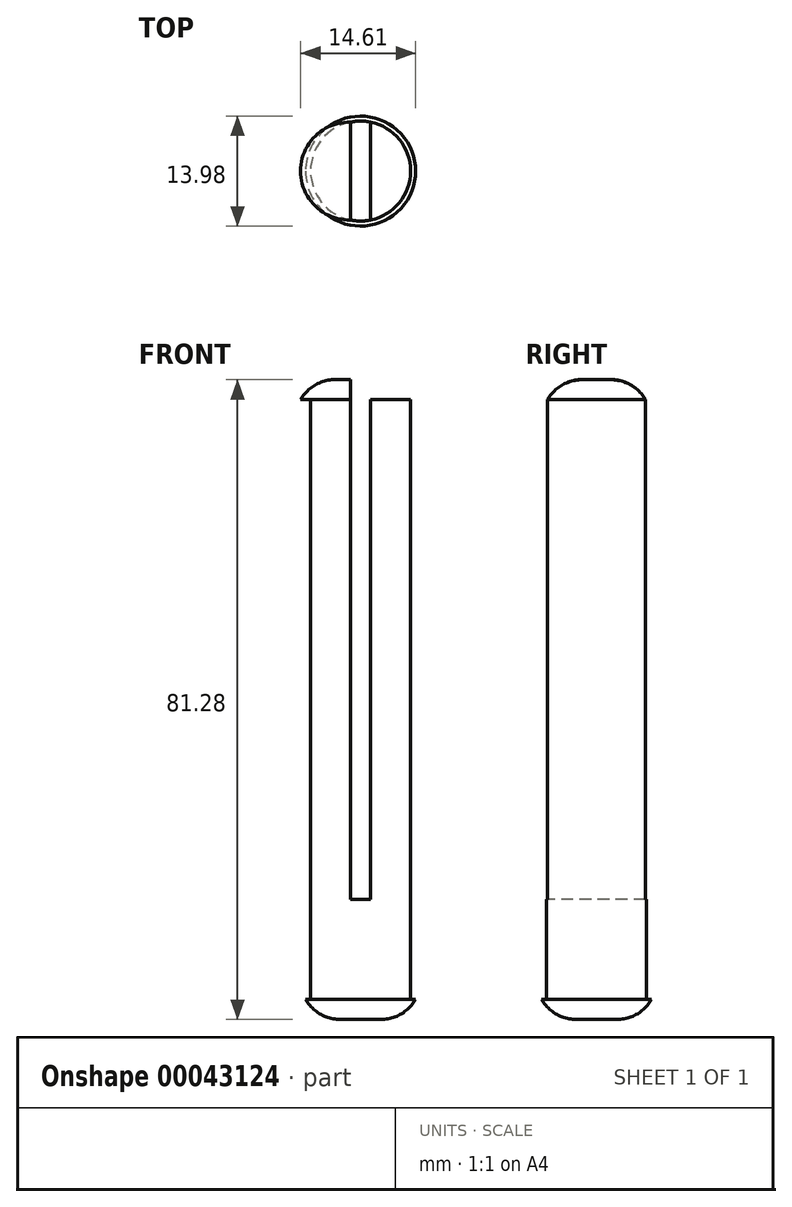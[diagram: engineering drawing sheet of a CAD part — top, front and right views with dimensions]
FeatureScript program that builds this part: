
annotation { "Feature Type Name" : "Feature", "Feature Type Description" : "" }
export const myFeature = defineFeature(function(context is Context, id is Id, definition is map)
    precondition{}
    {
        {
            var Q0;
            Q0=qCreatedBy(makeId("Top.planeOp"),FACE);
            var sketch = newSketch(context, id + "F0", { "sketchPlane" : qUnion([Q0])});
            skCircle(sketch, "E0", {"center": v(0, 0) * mm, "radius": 6.35 * mm});
            skSolve(sketch);
        }
        {
            var Q0;
            Q0=makeQuery(id+"F0.imprint","IMPRINT",FACE,{"disambiguationData":[TD([[makeQuery(id+"F0.imprint","IMPRINT",EDGE,{"derivedFrom":sQuery(id+"F0.wireOp",EDGE,"E0")}),1.0]])]});
            extrude(context, id + "F1", {"entities" : qUnion([Q0]), "depth" : 76.2 * mm});
        }
        {
            var Q0;
            Q0=makeQuery(id+"F1.opExtrude","CAP_FACE",FACE,{"disambiguationData":[OSD([sQuery(id+"F0.wireOp",EDGE,"E0")])],"isStart":false});
            var sketch = newSketch(context, id + "F2", { "sketchPlane" : qUnion([Q0])});
            skLineSegment(sketch, "E1.rect.bottom", {"start": v(1.27, 11.24) * mm, "end": v(-1.27, 11.24) * mm});
            skLineSegment(sketch, "E1.rect.top", {"start": v(1.27, -11.24) * mm, "end": v(-1.27, -11.24) * mm});
            skLineSegment(sketch, "E1.rect.left", {"start": v(1.27, 11.24) * mm, "end": v(1.27, -11.24) * mm});
            skLineSegment(sketch, "E1.rect.right", {"start": v(-1.27, 11.24) * mm, "end": v(-1.27, -11.24) * mm});
            skPoint(sketch, "E1.rect.middle", {"position": v(0, 0) * mm});
            skSolve(sketch);
        }
        {
            var Q0;
            {var subQ1=makeQuery(id+"F1.opExtrude","CAP_EDGE",EDGE,{"disambiguationData":[OSD([sQuery(id+"F0.wireOp",EDGE,"E0")])],"isStart":false});var subQ4=sQuery(id+"F2.wireOp",EDGE,"E1.rect.left");var subQ6=makeQuery(id+"F2.imprint","INTERSECT",VERTEX,{"disambiguationData":[OD(0.0)],"derivedFrom":[subQ1,subQ4]});Q0=makeQuery(id+"F2.imprint","IMPRINT",FACE,{"disambiguationData":[TD([[makeQuery(id+"F2.imprint","IMPRINT",EDGE,{"disambiguationData":[TD([[subQ6,-1.0]])],"derivedFrom":subQ4}),-1.0]])]});}
            extrude(context, id + "F3", {"entities" : qUnion([Q0]), "operationType" : NewBodyOperationType.REMOVE, "oppositeDirection" : true, "depth" : 63.5 * mm});
        }
        {
            var Q0;
            {var subQ0=sQuery(id+"F0.wireOp",EDGE,"E0");Q0=makeQuery(id+"F3.boolean.opBoolean","SPLIT",FACE,{"disambiguationData":[TD([makeQuery(id+"F3.opExtrude","SWEPT_FACE",FACE,{"disambiguationData":[OSD([sQuery(id+"F2.wireOp",EDGE,"E1.rect.right")])]})])],"derivedFrom":makeQuery(id+"F1.opExtrude","CAP_FACE",FACE,{"disambiguationData":[OSD([subQ0])],"isStart":false})});}
            var sketch = newSketch(context, id + "F4", { "sketchPlane" : qUnion([Q0])});
            skLineSegment(sketch, "E2", {"start": v(-8.9, 6.22) * mm, "end": v(-8.89, -19.18) * mm});
            skLineSegment(sketch, "E3", {"start": v(0, 6.22) * mm, "end": v(0, -19.9) * mm, "construction": true});
            skLineSegment(sketch, "E4.MirrorCS", {"start": v(8.9, 6.22) * mm, "end": v(8.89, -19.18) * mm});
            skArc(sketch, "E5", {"start": v(-1.27, 6.22) * mm, "mid": v(-7.62, 0) * mm, "end": v(-1.27, -6.22) * mm});
            skArc(sketch, "E6.MirrorCS", {"start": v(1.27, 6.22) * mm, "mid": v(7.62, 0) * mm, "end": v(1.27, -6.22) * mm});
            skLineSegment(sketch, "E7", {"start": v(1.27, 6.22) * mm, "end": v(1.27, -6.22) * mm});
            skLineSegment(sketch, "E8", {"start": v(-1.27, 6.22) * mm, "end": v(-1.27, -6.22) * mm});
            skSolve(sketch);
        }
        {
            var Q0;
            Q0=makeQuery(id+"F4.imprint","IMPRINT",FACE,{"disambiguationData":[TD([[makeQuery(id+"F4.imprint","IMPRINT",EDGE,{"derivedFrom":sQuery(id+"F4.wireOp",EDGE,"E5")}),1.0]])]});
            var Q1;
            Q1=makeQuery(id+"F4.imprint","IMPRINT",FACE,{"disambiguationData":[TD([[makeQuery(id+"F4.imprint","IMPRINT",EDGE,{"derivedFrom":sQuery(id+"F4.wireOp",EDGE,"E8")}),-1.0]])]});
            var Q2;
            Q2=makeQuery(id+"F4.imprint","IMPRINT",FACE,{"disambiguationData":[TD([[makeQuery(id+"F4.imprint","IMPRINT",EDGE,{"derivedFrom":sQuery(id+"F4.wireOp",EDGE,"E6.MirrorCS")}),-1.0]])]});
            extrude(context, id + "F5", {"entities" : qUnion([Q0, Q1, Q2]), "operationType" : NewBodyOperationType.ADD, "depth" : 2.54 * mm});
        }
        {
            var Q0;
            Q0=makeQuery(id+"F5.opExtrude","CAP_EDGE",EDGE,{"disambiguationData":[OSD([sQuery(id+"F4.wireOp",EDGE,"E5")])],"isStart":false});
            var Q1;
            Q1=makeQuery(id+"F5.opExtrude","CAP_EDGE",EDGE,{"disambiguationData":[OSD([sQuery(id+"F4.wireOp",EDGE,"E6.MirrorCS")])],"isStart":false});
            fillet(context, id + "F6", {"entities" : qUnion([Q0, Q1]), "radius" : 5.08 * mm, "tangentPropagation" : true, "allowEdgeOverflow" : false});
        }
        {
            var Q0;
            Q0=makeQuery(id+"F1.opExtrude","CAP_FACE",FACE,{"disambiguationData":[OSD([sQuery(id+"F0.wireOp",EDGE,"E0")])],"isStart":true});
            var sketch = newSketch(context, id + "F7", { "sketchPlane" : qUnion([Q0])});
            skCircle(sketch, "E9", {"center": v(0, 0) * mm, "radius": 6.99 * mm});
            skSolve(sketch);
        }
        {
            var Q0;
            Q0=makeQuery(id+"F7.imprint","IMPRINT",FACE,{"disambiguationData":[TD([[makeQuery(id+"F7.imprint","IMPRINT",EDGE,{"derivedFrom":sQuery(id+"F7.wireOp",EDGE,"E9")}),1.0]])]});
            var Q1;
            Q1=makeQuery(id+"F7.imprint","IMPRINT",FACE,{"disambiguationData":[TD([[makeQuery(id+"F7.imprint","IMPRINT",EDGE,{"derivedFrom":makeQuery(id+"F1.opExtrude","CAP_EDGE",EDGE,{"disambiguationData":[OSD([sQuery(id+"F0.wireOp",EDGE,"E0")])],"isStart":true})}),-1.0]])]});
            extrude(context, id + "F8", {"entities" : qUnion([Q0, Q1]), "operationType" : NewBodyOperationType.ADD, "depth" : 2.54 * mm});
        }
        {
            var Q0;
            Q0=makeQuery(id+"F8.opExtrude","CAP_FACE",FACE,{"disambiguationData":[OSD([sQuery(id+"F7.wireOp",EDGE,"E9")])],"isStart":false});
            fillet(context, id + "F9", {"entities" : qUnion([Q0]), "radius" : 5.08 * mm, "tangentPropagation" : true, "allowEdgeOverflow" : false});
        }
    });
